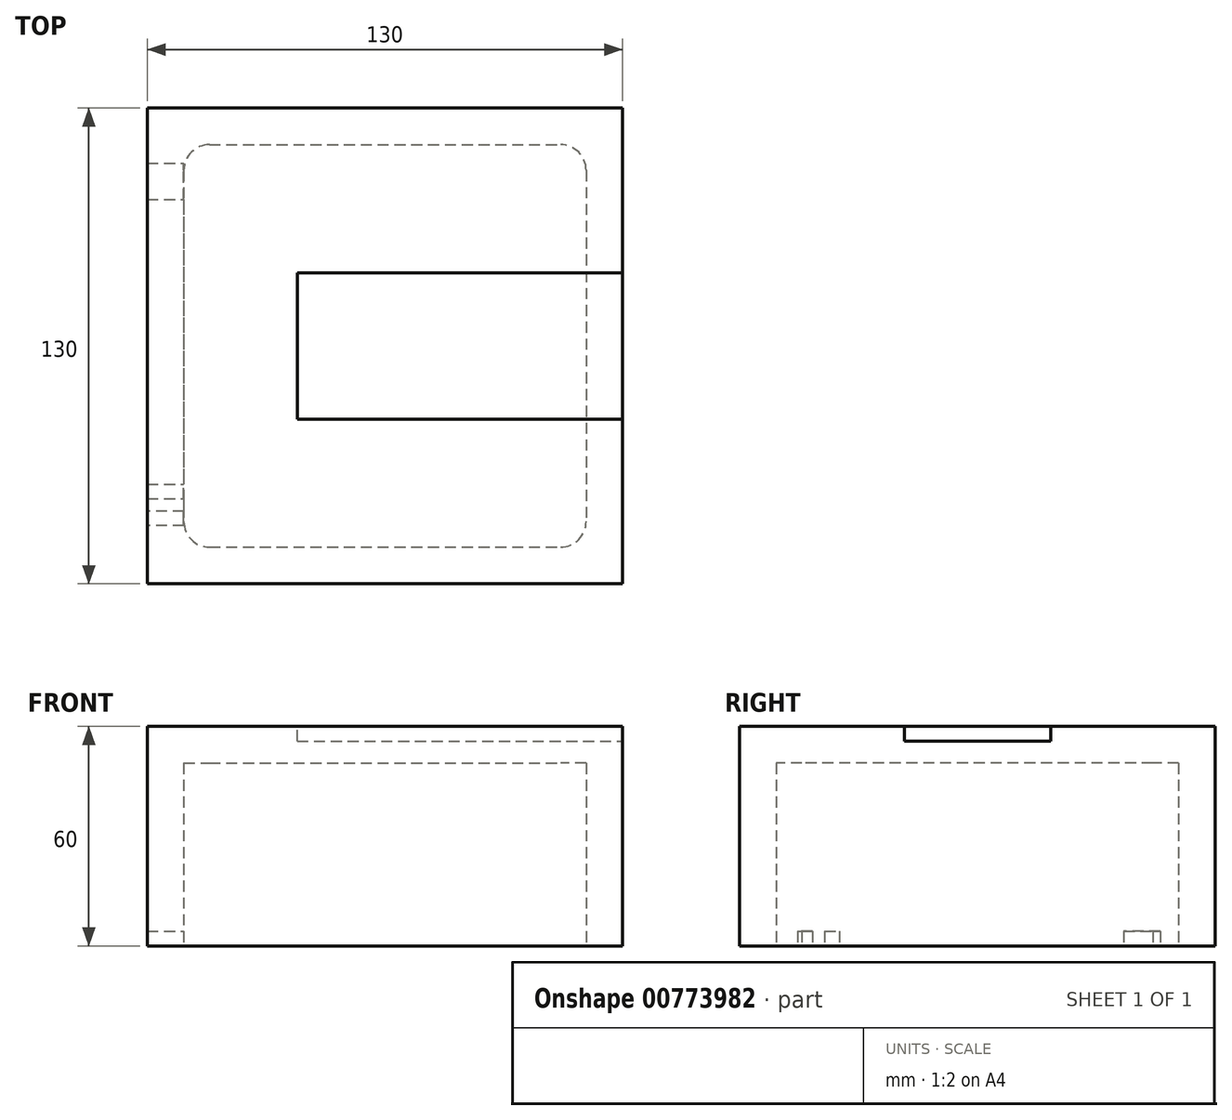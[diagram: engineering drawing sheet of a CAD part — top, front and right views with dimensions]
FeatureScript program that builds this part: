
annotation { "Feature Type Name" : "Feature", "Feature Type Description" : "" }
export const myFeature = defineFeature(function(context is Context, id is Id, definition is map)
    precondition{}
    {
        {
            var Q0;
            Q0=qCreatedBy(makeId("Top.planeOp"),FACE);
            var sketch = newSketch(context, id + "F0", { "sketchPlane" : qUnion([Q0])});
            skLineSegment(sketch, "E0.bottom", {"start": v(-65, 65) * mm, "end": v(65, 65) * mm});
            skLineSegment(sketch, "E0.top", {"start": v(-65, -65) * mm, "end": v(65, -65) * mm});
            skLineSegment(sketch, "E0.left", {"start": v(-65, 65) * mm, "end": v(-65, -65) * mm});
            skLineSegment(sketch, "E0.right", {"start": v(65, 65) * mm, "end": v(65, -65) * mm});
            skPoint(sketch, "E0.middle", {"position": v(0, 0) * mm});
            skSolve(sketch);
        }
        {
            var Q0;
            Q0 = qSketchRegion(id + "F0", true);
            extrude(context, id + "F1", {"entities" : qUnion([Q0]), "depth" : 60 * mm, "offsetDistance" : 25 * mm});
        }
        {
            var Q0;
            Q0=qCreatedBy(makeId("Top.planeOp"),FACE);
            var sketch = newSketch(context, id + "F2", { "sketchPlane" : qUnion([Q0])});
            skLineSegment(sketch, "E1.bottom", {"start": v(-55, 55) * mm, "end": v(55, 55) * mm});
            skLineSegment(sketch, "E1.top", {"start": v(-55, -55) * mm, "end": v(55, -55) * mm});
            skLineSegment(sketch, "E1.left", {"start": v(-55, 55) * mm, "end": v(-55, -55) * mm});
            skLineSegment(sketch, "E1.right", {"start": v(55, 55) * mm, "end": v(55, -55) * mm});
            skPoint(sketch, "E1.middle", {"position": v(0, 0) * mm});
            skSolve(sketch);
        }
        {
            var Q0;
            Q0=makeQuery(id+"F2.imprint","IMPRINT",FACE,{"disambiguationData":[TD([[makeQuery(id+"F2.imprint","IMPRINT",EDGE,{"derivedFrom":sQuery(id+"F2.wireOp",EDGE,"E1.bottom")}),-1.0]])]});
            extrude(context, id + "F3", {"entities" : qUnion([Q0]), "operationType" : NewBodyOperationType.REMOVE, "depth" : 50 * mm, "offsetDistance" : 25 * mm});
        }
        {
            var Q0;
            Q0=makeQuery(id+"F1.opExtrude","CAP_FACE",FACE,{"disambiguationData":[OSD([sQuery(id+"F0.wireOp",EDGE,"E0.bottom"),sQuery(id+"F0.wireOp",EDGE,"E0.top"),sQuery(id+"F0.wireOp",EDGE,"E0.left"),sQuery(id+"F0.wireOp",EDGE,"E0.right")])],"isStart":false});
            var sketch = newSketch(context, id + "F4", { "sketchPlane" : qUnion([Q0])});
            skLineSegment(sketch, "E2.bottom", {"start": v(-24, -20) * mm, "end": v(65, -20) * mm});
            skLineSegment(sketch, "E2.top", {"start": v(-24, 20) * mm, "end": v(65, 20) * mm});
            skLineSegment(sketch, "E2.left", {"start": v(-24, -20) * mm, "end": v(-24, 20) * mm});
            skLineSegment(sketch, "E2.right", {"start": v(65, -20) * mm, "end": v(65, 20) * mm});
            skSolve(sketch);
        }
        {
            var Q0;
            Q0 = qSketchRegion(id + "F4", true);
            extrude(context, id + "F5", {"entities" : qUnion([Q0]), "operationType" : NewBodyOperationType.REMOVE, "oppositeDirection" : true, "depth" : 4 * mm, "offsetDistance" : 25 * mm});
        }
        {
            var Q0;
            Q0=makeQuery(id+"F3.boolean.opBoolean","COPY",EDGE,{"derivedFrom":makeQuery(id+"F3.opExtrude","SWEPT_EDGE",EDGE,{"disambiguationData":[OSD([sQuery(id+"F2.wireOp",EDGE,"E1.top"),sQuery(id+"F2.wireOp",EDGE,"E1.right")])]})});
            var Q1;
            Q1=makeQuery(id+"F3.boolean.opBoolean","COPY",EDGE,{"derivedFrom":makeQuery(id+"F3.opExtrude","SWEPT_EDGE",EDGE,{"disambiguationData":[OSD([sQuery(id+"F2.wireOp",EDGE,"E1.bottom"),sQuery(id+"F2.wireOp",EDGE,"E1.right")])]})});
            var Q2;
            Q2=makeQuery(id+"F3.boolean.opBoolean","COPY",EDGE,{"derivedFrom":makeQuery(id+"F3.opExtrude","SWEPT_EDGE",EDGE,{"disambiguationData":[OSD([sQuery(id+"F2.wireOp",EDGE,"E1.bottom"),sQuery(id+"F2.wireOp",EDGE,"E1.left")])]})});
            var Q3;
            Q3=makeQuery(id+"F3.boolean.opBoolean","COPY",EDGE,{"derivedFrom":makeQuery(id+"F3.opExtrude","SWEPT_EDGE",EDGE,{"disambiguationData":[OSD([sQuery(id+"F2.wireOp",EDGE,"E1.top"),sQuery(id+"F2.wireOp",EDGE,"E1.left")])]})});
            fillet(context, id + "F6", {"entities" : qUnion([Q0, Q1, Q2, Q3]), "radius" : 7 * mm, "tangentPropagation" : true, "allowEdgeOverflow" : false});
        }
        {
            var Q0;
            Q0=makeQuery(id+"F0.imprint","IMPRINT",FACE,{"disambiguationData":[TD([[makeQuery(id+"F0.imprint","IMPRINT",EDGE,{"derivedFrom":sQuery(id+"F0.wireOp",EDGE,"E0.bottom")}),-1.0]])]});
            var sketch = newSketch(context, id + "F7", { "sketchPlane" : qUnion([Q0])});
            skLineSegment(sketch, "E3.bottom", {"start": v(-65, -41.78) * mm, "end": v(-55, -41.78) * mm});
            skLineSegment(sketch, "E3.top", {"start": v(-65, -37.78) * mm, "end": v(-55, -37.78) * mm});
            skLineSegment(sketch, "E3.left", {"start": v(-65, -41.78) * mm, "end": v(-65, -37.78) * mm});
            skLineSegment(sketch, "E3.right", {"start": v(-55, -41.78) * mm, "end": v(-55, -37.78) * mm});
            skPoint(sketch, "E3.middle", {"position": v(-60, -39.78) * mm});
            skSolve(sketch);
        }
        {
            var Q0;
            Q0 = qSketchRegion(id + "F7", true);
            extrude(context, id + "F8", {"entities" : qUnion([Q0]), "operationType" : NewBodyOperationType.REMOVE, "depth" : 4 * mm, "offsetDistance" : 25 * mm});
        }
        {
            var Q0;
            Q0=makeQuery(id+"F0.imprint","IMPRINT",FACE,{"disambiguationData":[TD([[makeQuery(id+"F0.imprint","IMPRINT",EDGE,{"derivedFrom":sQuery(id+"F0.wireOp",EDGE,"E0.bottom")}),-1.0]])]});
            var sketch = newSketch(context, id + "F9", { "sketchPlane" : qUnion([Q0])});
            skLineSegment(sketch, "E4.bottom", {"start": v(-55, -49.14) * mm, "end": v(-65, -49.14) * mm});
            skLineSegment(sketch, "E4.top", {"start": v(-55, -45.14) * mm, "end": v(-65, -45.14) * mm});
            skLineSegment(sketch, "E4.left", {"start": v(-55, -49.14) * mm, "end": v(-55, -45.14) * mm});
            skLineSegment(sketch, "E4.right", {"start": v(-65, -49.14) * mm, "end": v(-65, -45.14) * mm});
            skSolve(sketch);
        }
        {
            var Q0;
            Q0 = qSketchRegion(id + "F9", true);
            extrude(context, id + "F10", {"entities" : qUnion([Q0]), "operationType" : NewBodyOperationType.REMOVE, "depth" : 4 * mm, "offsetDistance" : 25 * mm});
        }
        {
            var Q0;
            Q0=makeQuery(id+"F0.imprint","IMPRINT",FACE,{"disambiguationData":[TD([[makeQuery(id+"F0.imprint","IMPRINT",EDGE,{"derivedFrom":sQuery(id+"F0.wireOp",EDGE,"E0.bottom")}),-1.0]])]});
            var sketch = newSketch(context, id + "F11", { "sketchPlane" : qUnion([Q0])});
            skLineSegment(sketch, "E5.bottom", {"start": v(-65, 50) * mm, "end": v(-55, 50) * mm});
            skLineSegment(sketch, "E5.top", {"start": v(-65, 40) * mm, "end": v(-55, 40) * mm});
            skLineSegment(sketch, "E5.left", {"start": v(-65, 40) * mm, "end": v(-65, 50) * mm});
            skLineSegment(sketch, "E5.right", {"start": v(-55, 40) * mm, "end": v(-55, 50) * mm});
            skSolve(sketch);
        }
        {
            var Q0;
            Q0 = qSketchRegion(id + "F11", true);
            extrude(context, id + "F12", {"entities" : qUnion([Q0]), "operationType" : NewBodyOperationType.REMOVE, "depth" : 4 * mm, "offsetDistance" : 25 * mm});
        }
    });
